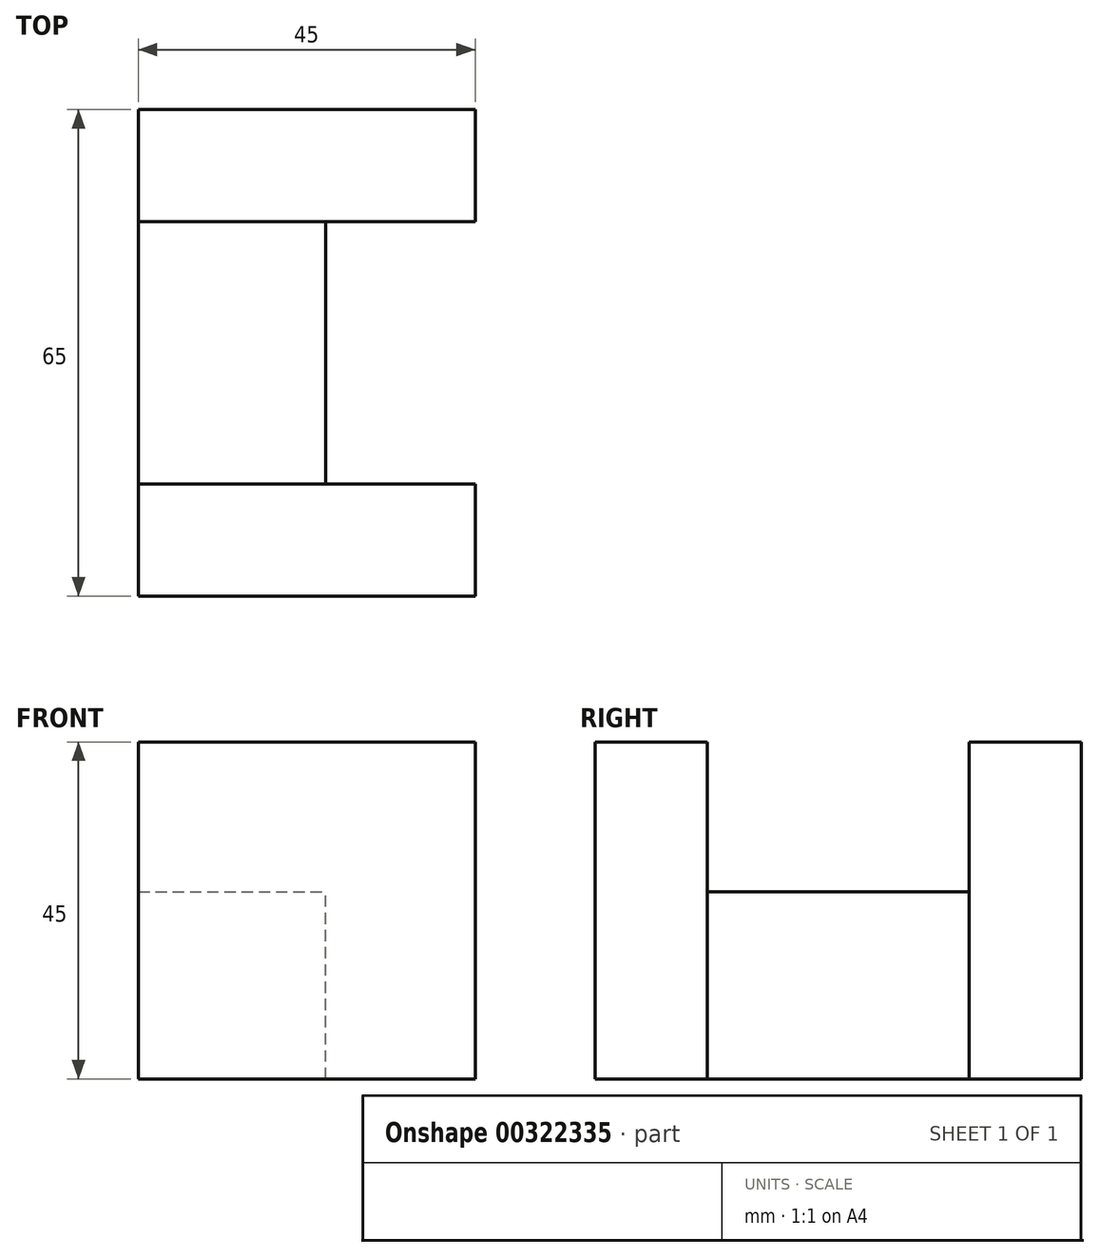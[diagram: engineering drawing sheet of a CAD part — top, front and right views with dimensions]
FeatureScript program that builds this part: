
annotation { "Feature Type Name" : "Feature", "Feature Type Description" : "" }
export const myFeature = defineFeature(function(context is Context, id is Id, definition is map)
    precondition{}
    {
        {
            var Q0;
            Q0=qCreatedBy(makeId("Front.planeOp"),FACE);
            var sketch = newSketch(context, id + "F0", { "sketchPlane" : qUnion([Q0])});
            skLineSegment(sketch, "E0.bottom", {"start": v(0, 0) * mm, "end": v(25, 0) * mm});
            skLineSegment(sketch, "E0.top", {"start": v(0, 25) * mm, "end": v(25, 25) * mm});
            skLineSegment(sketch, "E0.left", {"start": v(0, 0) * mm, "end": v(0, 25) * mm});
            skLineSegment(sketch, "E0.right", {"start": v(25, 0) * mm, "end": v(25, 25) * mm});
            skSolve(sketch);
        }
        {
            var Q0;
            Q0=makeQuery(id+"F0.imprint","IMPRINT",FACE,{"disambiguationData":[TD([[makeQuery(id+"F0.imprint","IMPRINT",EDGE,{"derivedFrom":sQuery(id+"F0.wireOp",EDGE,"E0.bottom")}),1.0]])]});
            extrude(context, id + "F1", {"entities" : qUnion([Q0]), "depth" : 17.5 * mm});
        }
        {
            var Q0;
            Q0=makeQuery(id+"F1.opExtrude","CAP_FACE",FACE,{"disambiguationData":[OSD([sQuery(id+"F0.wireOp",EDGE,"E0.bottom"),sQuery(id+"F0.wireOp",EDGE,"E0.top"),sQuery(id+"F0.wireOp",EDGE,"E0.left"),sQuery(id+"F0.wireOp",EDGE,"E0.right")])],"isStart":false});
            var sketch = newSketch(context, id + "F2", { "sketchPlane" : qUnion([Q0])});
            skLineSegment(sketch, "E1.bottom", {"start": v(0, 0) * mm, "end": v(45, 0) * mm});
            skLineSegment(sketch, "E1.top", {"start": v(0, 45) * mm, "end": v(45, 45) * mm});
            skLineSegment(sketch, "E1.left", {"start": v(0, 0) * mm, "end": v(0, 45) * mm});
            skLineSegment(sketch, "E1.right", {"start": v(45, 0) * mm, "end": v(45, 45) * mm});
            skSolve(sketch);
        }
        {
            var Q0;
            {var subQ3=sQuery(id+"F2.wireOp",EDGE,"E1.top");Q0=makeQuery(id+"F2.imprint","IMPRINT",FACE,{"disambiguationData":[TD([[makeQuery(id+"F2.imprint","IMPRINT",EDGE,{"derivedFrom":subQ3}),-1.0]])]});}
            var Q1;
            {var subQ4=makeQuery(id+"F1.opExtrude","CAP_EDGE",EDGE,{"disambiguationData":[OSD([sQuery(id+"F0.wireOp",EDGE,"E0.top")])],"isStart":false});Q1=makeQuery(id+"F2.imprint","IMPRINT",FACE,{"disambiguationData":[TD([[makeQuery(id+"F2.imprint","IMPRINT",EDGE,{"derivedFrom":subQ4}),-1.0]])]});}
            extrude(context, id + "F3", {"entities" : qUnion([Q0, Q1]), "operationType" : NewBodyOperationType.ADD, "depth" : 15 * mm});
        }
        {
            var Q0;
            Q0=makeQuery(id+"F1.opExtrude","SWEPT_BODY",BODY,{"disambiguationData":[OSD([sQuery(id+"F0.wireOp",EDGE,"E0.bottom"),sQuery(id+"F0.wireOp",EDGE,"E0.top"),sQuery(id+"F0.wireOp",EDGE,"E0.left"),sQuery(id+"F0.wireOp",EDGE,"E0.right")])]});
            var Q1;
            Q1=makeQuery(id+"F1.opExtrude","CAP_FACE",FACE,{"disambiguationData":[OSD([sQuery(id+"F0.wireOp",EDGE,"E0.bottom"),sQuery(id+"F0.wireOp",EDGE,"E0.top"),sQuery(id+"F0.wireOp",EDGE,"E0.left"),sQuery(id+"F0.wireOp",EDGE,"E0.right")])],"isStart":true});
            mirror(context, id + "F4", {"operationType" : NewBodyOperationType.ADD, "entities" : qUnion([Q0]), "mirrorPlane" : qUnion([Q1])});
        }
    });
